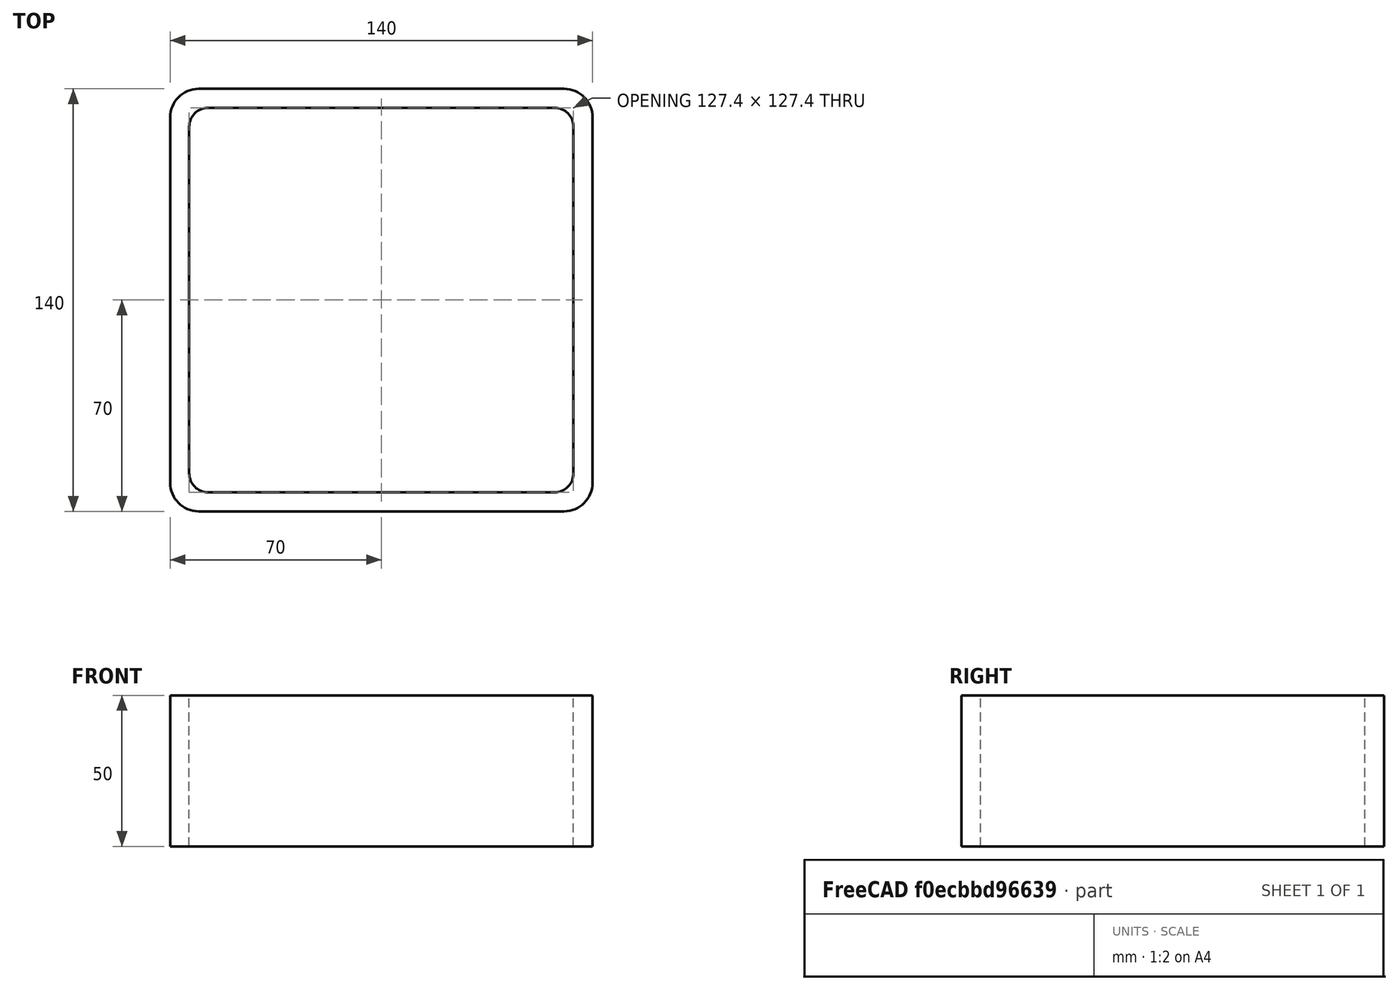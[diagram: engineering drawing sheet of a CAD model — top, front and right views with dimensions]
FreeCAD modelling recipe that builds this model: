
FCSTD DOCUMENT  (FreeCAD 0.15R4671 (Git))
Label: Square hollow section 140x140x6.3 EN10219 S235JRH
License: All rights reserved
LicenseURL: http://en.wikipedia.org/wiki/All_rights_reserved
objects: Sketcher::SketchObject×1, Part::Extrusion×1
note: 2 computed .brp shape members not serialized (recipe doc carries the construction recipe); baked Part::Feature solids carry a one-line shape summary decoded from their .brp

FEATURE [Sketcher::SketchObject] Sketch
  sketch-geometry (16):
    g0: LineSegment StartX=-57.4 StartY=63.7 StartZ=0 EndX=57.4 EndY=63.7 EndZ=0
    g1: LineSegment StartX=63.7 StartY=57.4 StartZ=0 EndX=63.7 EndY=-57.4 EndZ=0
    g2: LineSegment StartX=57.4 StartY=-63.7 StartZ=0 EndX=-57.4 EndY=-63.7 EndZ=0
    g3: LineSegment StartX=-63.7 StartY=-57.4 StartZ=0 EndX=-63.7 EndY=57.4 EndZ=0
    g4: LineSegment StartX=-60.55 StartY=70 StartZ=0 EndX=60.55 EndY=70 EndZ=0
    g5: LineSegment StartX=70 StartY=60.55 StartZ=0 EndX=70 EndY=-60.55 EndZ=0
    g6: LineSegment StartX=60.55 StartY=-70 StartZ=0 EndX=-60.55 EndY=-70 EndZ=0
    g7: LineSegment StartX=-70 StartY=-60.55 StartZ=0 EndX=-70 EndY=60.55 EndZ=0
    g8: ArcOfCircle CenterX=-57.4 CenterY=57.4 CenterZ=0 NormalX=0 NormalY=0 NormalZ=1 Radius=6.3 StartAngle=1.5708 EndAngle=3.14159
    g9: ArcOfCircle CenterX=57.4 CenterY=57.4 CenterZ=0 NormalX=0 NormalY=0 NormalZ=1 Radius=6.3 StartAngle=0 EndAngle=1.5708
    g10: ArcOfCircle CenterX=57.4 CenterY=-57.4 CenterZ=0 NormalX=0 NormalY=0 NormalZ=1 Radius=6.3 StartAngle=4.71239 EndAngle=6.28319
    g11: ArcOfCircle CenterX=-57.4 CenterY=-57.4 CenterZ=0 NormalX=0 NormalY=0 NormalZ=1 Radius=6.3 StartAngle=3.14159 EndAngle=4.71239
    g12: ArcOfCircle CenterX=60.55 CenterY=60.55 CenterZ=0 NormalX=0 NormalY=0 NormalZ=1 Radius=9.45 StartAngle=0 EndAngle=1.5708
    g13: ArcOfCircle CenterX=60.55 CenterY=-60.55 CenterZ=0 NormalX=0 NormalY=0 NormalZ=1 Radius=9.45 StartAngle=4.71239 EndAngle=6.28319
    g14: ArcOfCircle CenterX=-60.55 CenterY=-60.55 CenterZ=0 NormalX=0 NormalY=0 NormalZ=1 Radius=9.45 StartAngle=3.14159 EndAngle=4.71239
    g15: ArcOfCircle CenterX=-60.55 CenterY=60.55 CenterZ=0 NormalX=0 NormalY=0 NormalZ=1 Radius=9.45 StartAngle=1.5708 EndAngle=3.14159
  constraints (36):
    c: Horizontal(g2)
    c: Vertical(g3)
    c: Horizontal(g6)
    c: Vertical(g7)
    c: Tangent(g3,g8) = 1.5708
    c: Tangent(g0,g8) = 1.5708
    c: Tangent(g0,g9) = 1.5708
    c: Tangent(g1,g9) = 1.5708
    c: Tangent(g1,g10) = 1.5708
    c: Tangent(g2,g10) = 1.5708
    c: Tangent(g2,g11) = 1.5708
    c: Tangent(g3,g11) = 1.5708
    c: Tangent(g4,g12) = 1.5708
    c: Tangent(g5,g12) = 1.5708
    c: Tangent(g5,g13) = 1.5708
    c: Tangent(g6,g13) = 1.5708
    c: Tangent(g6,g14) = 1.5708
    c: Tangent(g7,g14) = 1.5708
    c: Tangent(g7,g15) = 1.5708
    c: Tangent(g4,g15) = 1.5708
    c: Equal(g9,g8)
    c: Equal(g9,g11)
    c: Equal(g9,g10)
    c: Equal(g12,g15)
    c: Equal(g12,g14)
    c: Equal(g12,g13)
    c: Symmetric(g4,g6,g-1)
    c: Symmetric(g7,g5,g-2)
    c: DistanceY(g4,g6) = -140
    c: DistanceX(g7,g5) = 140
    c: Symmetric(g3,g1,g-2)
    c: Symmetric(g0,g2,g-1)
    c: DistanceY(g0,g4) = 6.3
    c: DistanceX(g5,g1) = -6.3
    c: Radius(g9) = 6.3
    c: Radius(g12) = 9.45
FEATURE [Part::Extrusion] Extrude  label="Square hollow section 140x140x6.3 EN10219 S235JRH"
  Base = -> Sketch
  Dir = (0,0,50)
  Solid = true
